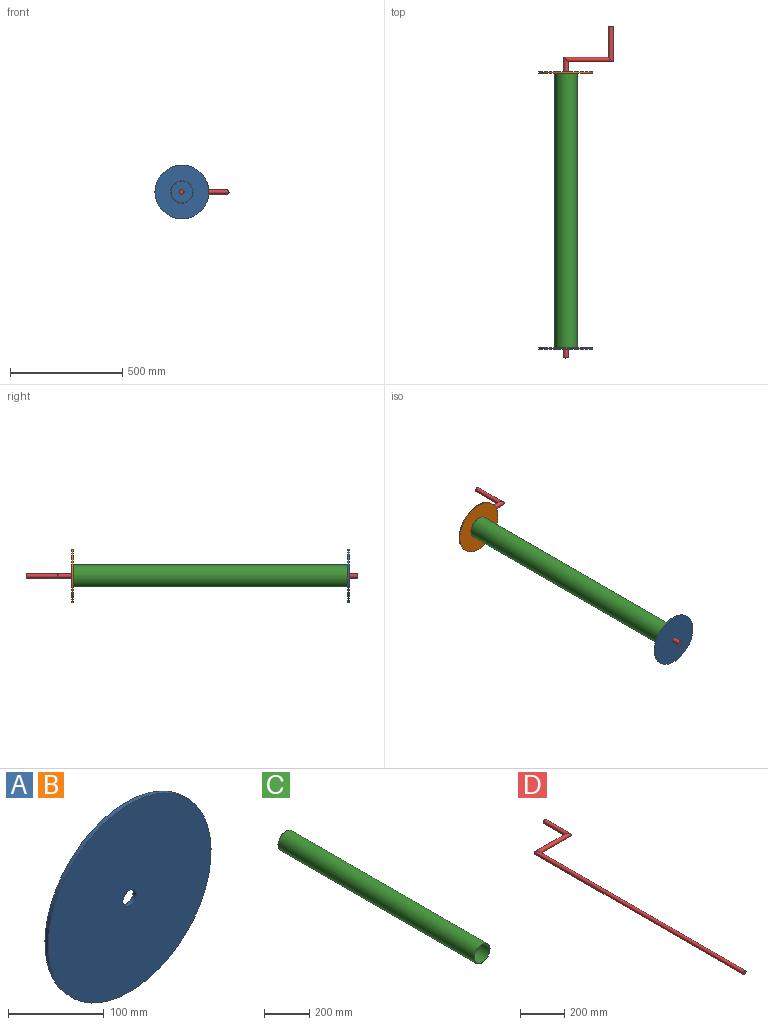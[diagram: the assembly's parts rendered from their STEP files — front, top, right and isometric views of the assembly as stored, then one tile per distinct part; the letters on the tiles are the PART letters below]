
ASSEMBLY  parts=4 mates=3
PART A: 4 faces, bbox 240x5x240 mm
  f0: cylinder r=10mm len=20mm, axis (0,1,0), area 314.2mm2, adj f2,f3
  f1: cylinder r=120mm len=240mm, axis (0,1,0), area 3769.9mm2, adj f2,f3
  f2: plane 240x240mm, normal (0,-1,0), area 44924.8mm2, adj f0,f1
  f3: plane 240x240mm, normal (0,1,0), area 44924.8mm2, adj f0,f1
PART B: same geometry as A
PART C: 4 faces, bbox 100x1225x100 mm
  f0: cylinder r=48.2mm len=1225mm, axis (0,1,0), area 370990.7mm2, adj f2,f3
  f1: cylinder r=50mm len=1225mm, axis (0,1,0), area 384845.1mm2, adj f2,f3
  f2: plane 100x100mm, normal (0,-1,0), area 555.3mm2, adj f0,f1
  f3: plane 100x100mm, normal (0,1,0), area 555.3mm2, adj f0,f1
PART D: 5 faces, bbox 220x1480x20 mm
  f0: cylinder r=10mm len=1340.01mm, axis (0,1,0), area 83566.4mm2, adj f1,f4
  f1: plane 20x20mm, normal (0,-1,0), area 314.2mm2, adj f0
  f2: plane 20x20mm, normal (0,1,0), area 314.2mm2, adj f3
  f3: cylinder r=10mm len=160mm, axis (0,1,0), area 9424.8mm2, adj f2,f4
  f4: cylinder r=10mm len=220.01mm, axis (1,0,0), area 12566.4mm2, adj f0,f3
PLACE A rot(axis=(1,0,0),180deg) t=(-67.27,-744.74,-181.36)mm
PLACE B t=(-67.27,490.26,-181.36)mm
PLACE C rot(axis=(1,0,0),180deg) t=(-67.27,-739.74,-181.36)mm
PLACE D t=(-67.27,505.26,-181.36)mm
MATE fastened A.f1 <-> B.f1  axis (0,1,0) through (-67.27,-739.74,-181.36)mm
MATE fastened C.f0 <-> B.f1  axis (0,1,0) through (-67.27,485.26,-181.36)mm
MATE fastened D.f0 <-> A.f1  axis (0,-1,0) through (-67.27,-784.74,-181.36)mm
